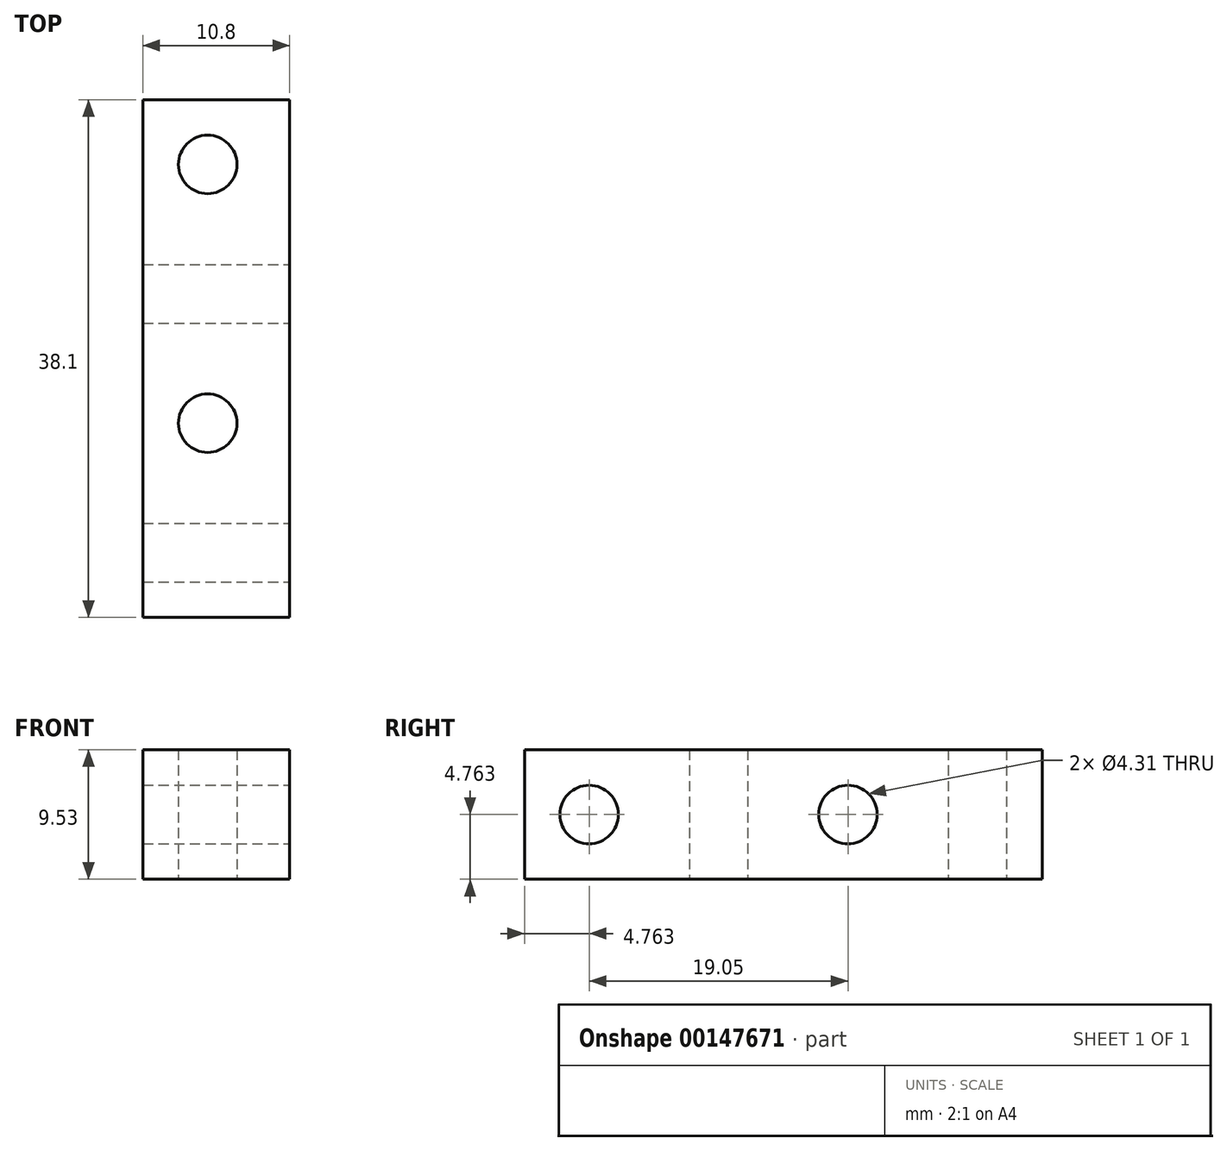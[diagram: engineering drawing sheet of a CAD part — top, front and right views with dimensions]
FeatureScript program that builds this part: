
annotation { "Feature Type Name" : "Feature", "Feature Type Description" : "" }
export const myFeature = defineFeature(function(context is Context, id is Id, definition is map)
    precondition{}
    {
        {
            var Q0;
            Q0=qCreatedBy(makeId("Top.planeOp"),FACE);
            var sketch = newSketch(context, id + "F0", { "sketchPlane" : qUnion([Q0])});
            skLineSegment(sketch, "E0.bottom", {"start": v(0, 0) * mm, "end": v(10.8, 0) * mm});
            skLineSegment(sketch, "E0.top", {"start": v(0, -38.1) * mm, "end": v(10.8, -38.1) * mm});
            skLineSegment(sketch, "E0.left", {"start": v(0, 0) * mm, "end": v(0, -38.1) * mm});
            skLineSegment(sketch, "E0.right", {"start": v(10.8, 0) * mm, "end": v(10.8, -38.1) * mm});
            skLineSegment(sketch, "E1", {"start": v(4.76, 0) * mm, "end": v(4.76, -4.76) * mm, "construction": true});
            skLineSegment(sketch, "E2", {"start": v(4.76, -4.76) * mm, "end": v(4.76, -23.81) * mm, "construction": true});
            skLineSegment(sketch, "E3", {"start": v(4.76, -23.81) * mm, "end": v(4.76, -38.1) * mm, "construction": true});
            skLineSegment(sketch, "E4", {"start": v(4.76, -4.76) * mm, "end": v(0, -4.76) * mm, "construction": true});
            skCircle(sketch, "E5", {"center": v(4.76, -4.76) * mm, "radius": 2.15 * mm});
            skCircle(sketch, "E6", {"center": v(4.76, -23.81) * mm, "radius": 2.15 * mm});
            skSolve(sketch);
        }
        {
            var Q0;
            Q0=qSketchRegion(id+"F0",true);
            extrude(context, id + "F1", {"entities" : qUnion([Q0]), "depth" : 9.52 * mm});
        }
        {
            var Q0;
            Q0=makeQuery(id+"F1.opExtrude","SWEPT_FACE",FACE,{"disambiguationData":[OSD([sQuery(id+"F0.wireOp",EDGE,"E0.right")])]});
            var sketch = newSketch(context, id + "F2", { "sketchPlane" : qUnion([Q0])});
            skLineSegment(sketch, "E7", {"start": v(0, 4.76) * mm, "end": v(-14.29, 4.76) * mm, "construction": true});
            skLineSegment(sketch, "E8", {"start": v(-38.1, 4.76) * mm, "end": v(-33.34, 4.76) * mm, "construction": true});
            skCircle(sketch, "E9", {"center": v(-33.34, 4.76) * mm, "radius": 2.15 * mm});
            skCircle(sketch, "E10", {"center": v(-14.29, 4.76) * mm, "radius": 2.15 * mm});
            skSolve(sketch);
        }
        {
            var Q0;
            Q0=qSketchRegion(id+"F2",true);
            var Q1;
            Q1=makeQuery(id+"F1.opExtrude","SWEPT_FACE",FACE,{"disambiguationData":[OSD([sQuery(id+"F0.wireOp",EDGE,"E0.left")])]});
            extrude(context, id + "F3", {"entities" : qUnion([Q0]), "operationType" : NewBodyOperationType.REMOVE, "endBound" : BoundingType.UP_TO_SURFACE, "oppositeDirection" : true, "endBoundEntityFace" : qUnion([Q1]), "depth" : 25.4 * mm});
        }
    });
